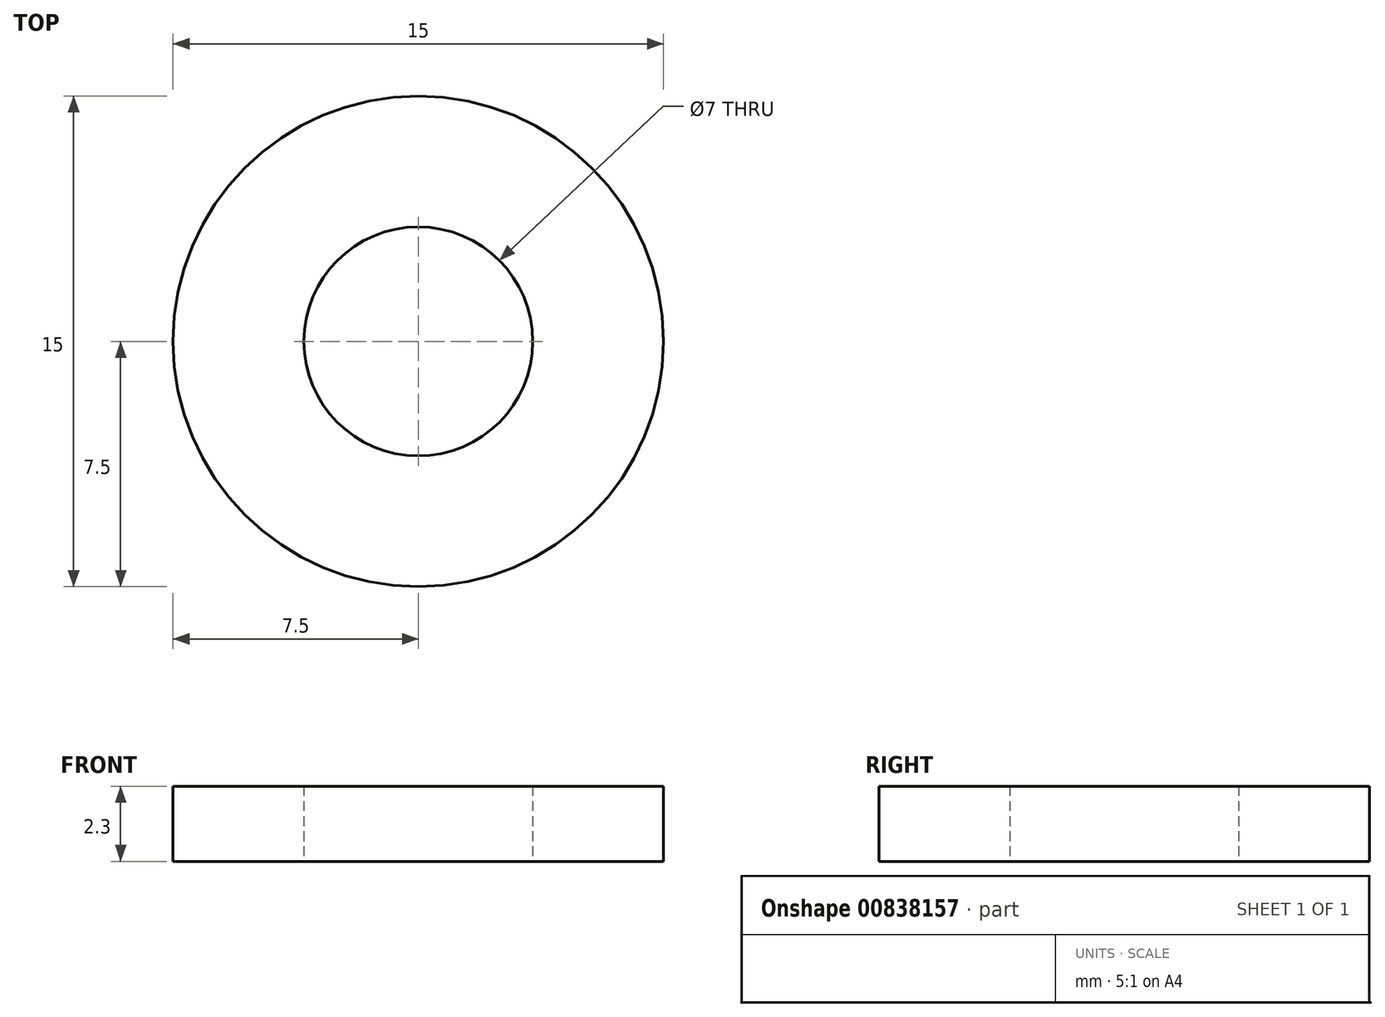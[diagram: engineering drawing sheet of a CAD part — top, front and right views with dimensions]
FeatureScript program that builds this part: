
annotation { "Feature Type Name" : "Feature", "Feature Type Description" : "" }
export const myFeature = defineFeature(function(context is Context, id is Id, definition is map)
    precondition{}
    {
        {
            var Q0;
            Q0=qCreatedBy(makeId("Top.planeOp"),FACE);
            var sketch = newSketch(context, id + "F0", { "sketchPlane" : qUnion([Q0])});
            skCircle(sketch, "E0", {"center": v(0, 0) * mm, "radius": 7.5 * mm});
            skCircle(sketch, "E1", {"center": v(0, 0) * mm, "radius": 3.5 * mm});
            skSolve(sketch);
        }
        {
            var Q0;
            Q0=makeQuery(id+"F0.imprint","IMPRINT",FACE,{"disambiguationData":[TD([[makeQuery(id+"F0.imprint","IMPRINT",EDGE,{"derivedFrom":sQuery(id+"F0.wireOp",EDGE,"E0")}),1.0]])]});
            extrude(context, id + "F1", {"entities" : qUnion([Q0]), "depth" : 2.3 * mm, "offsetDistance" : 25 * mm});
        }
    });
